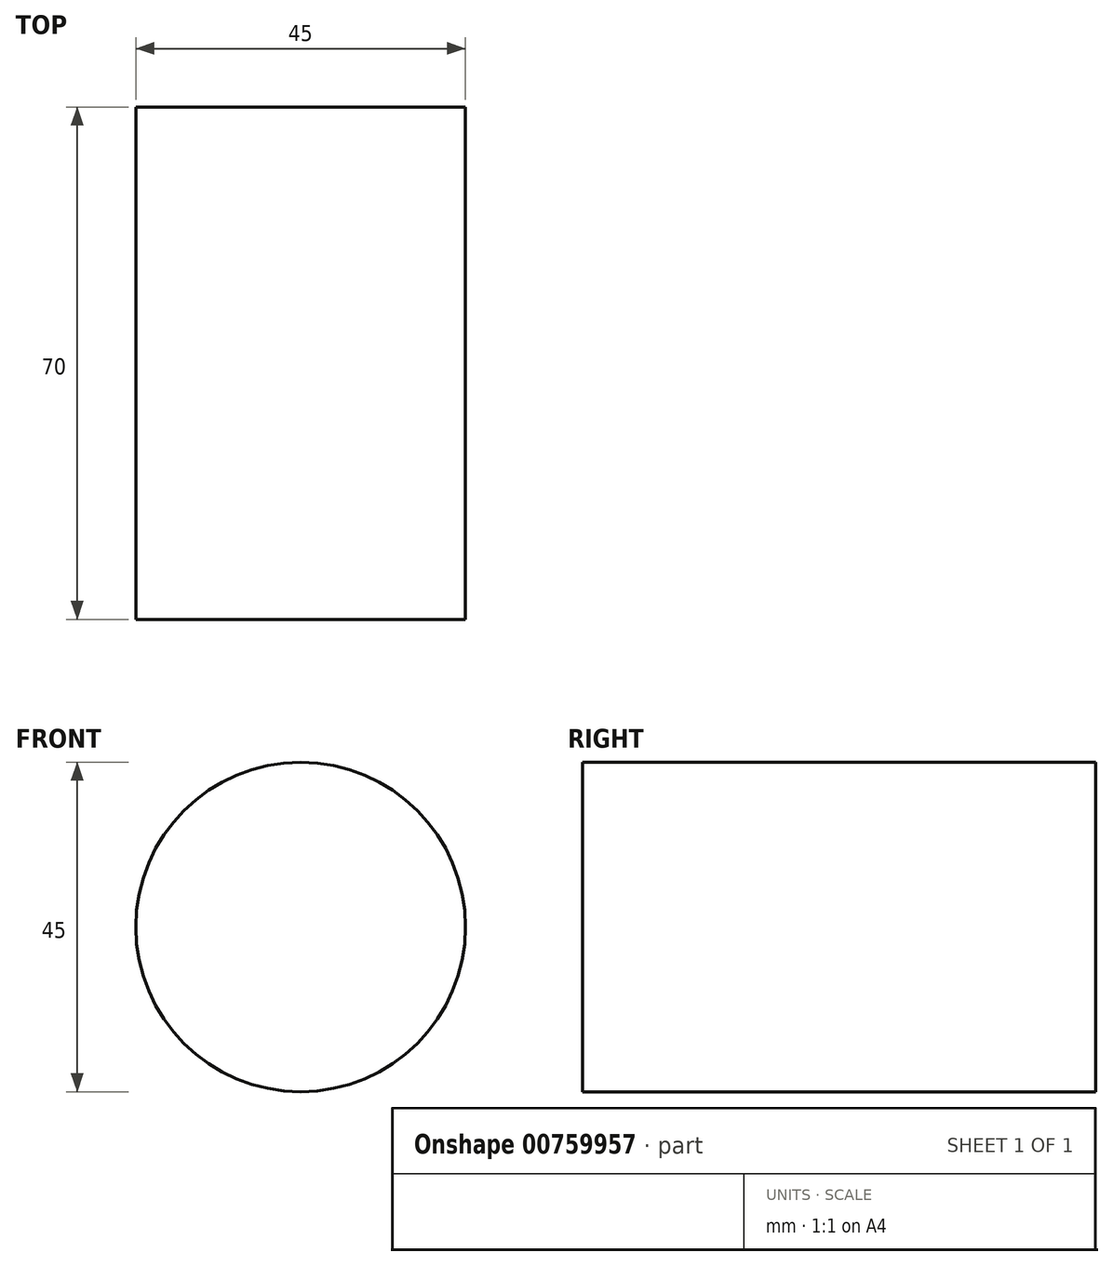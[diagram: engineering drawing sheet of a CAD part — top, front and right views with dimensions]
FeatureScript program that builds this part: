
annotation { "Feature Type Name" : "Feature", "Feature Type Description" : "" }
export const myFeature = defineFeature(function(context is Context, id is Id, definition is map)
    precondition{}
    {
        {
            var Q0;
            Q0=qCreatedBy(makeId("Front.planeOp"),FACE);
            var sketch = newSketch(context, id + "F0", { "sketchPlane" : qUnion([Q0])});
            skCircle(sketch, "E0", {"center": v(0, 0) * mm, "radius": 22.5 * mm});
            skSolve(sketch);
        }
        {
            var Q0;
            Q0=makeQuery(id+"F0.imprint","IMPRINT",FACE,{"disambiguationData":[TD([[makeQuery(id+"F0.imprint","IMPRINT",EDGE,{"derivedFrom":sQuery(id+"F0.wireOp",EDGE,"E0")}),1.0]])]});
            extrude(context, id + "F1", {"entities" : qUnion([Q0]), "depth" : 70 * mm, "offsetDistance" : 25 * mm});
        }
    });
